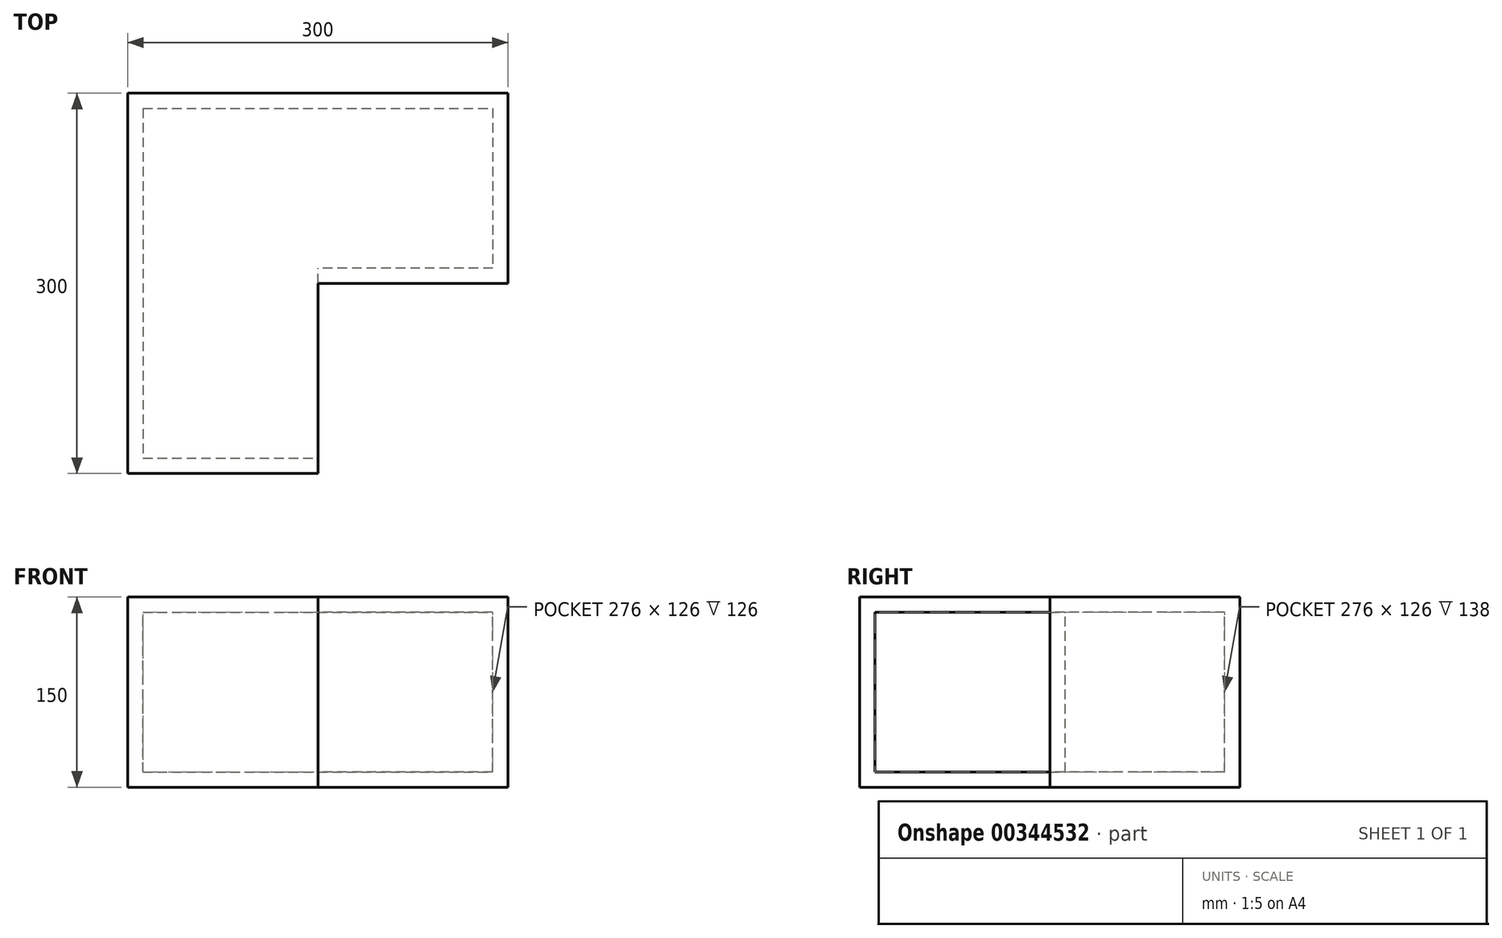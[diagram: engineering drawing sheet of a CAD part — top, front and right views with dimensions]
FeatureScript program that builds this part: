
annotation { "Feature Type Name" : "Feature", "Feature Type Description" : "" }
export const myFeature = defineFeature(function(context is Context, id is Id, definition is map)
    precondition{}
    {
        {
            var Q0;
            Q0=qCreatedBy(makeId("Top.planeOp"),FACE);
            var sketch = newSketch(context, id + "F0", { "sketchPlane" : qUnion([Q0])});
            skLineSegment(sketch, "E0.bottom", {"start": v(-150, 150) * mm, "end": v(150, 150) * mm});
            skLineSegment(sketch, "E0.top", {"start": v(-150, -150) * mm, "end": v(150, -150) * mm});
            skLineSegment(sketch, "E0.left", {"start": v(-150, 150) * mm, "end": v(-150, -150) * mm});
            skLineSegment(sketch, "E0.right", {"start": v(150, 150) * mm, "end": v(150, -150) * mm});
            skPoint(sketch, "E0.middle", {"position": v(0, 0) * mm});
            skLineSegment(sketch, "E1.bottom", {"start": v(150, -150) * mm, "end": v(0, -150) * mm});
            skLineSegment(sketch, "E1.top", {"start": v(150, 0) * mm, "end": v(0, 0) * mm});
            skLineSegment(sketch, "E1.left", {"start": v(150, -150) * mm, "end": v(150, 0) * mm});
            skLineSegment(sketch, "E1.right", {"start": v(0, -150) * mm, "end": v(0, 0) * mm});
            skSolve(sketch);
        }
        {
            var Q0;
            Q0=makeQuery(id+"F0.imprint","IMPRINT",FACE,{"disambiguationData":[TD([[makeQuery(id+"F0.imprint","IMPRINT",EDGE,{"derivedFrom":sQuery(id+"F0.wireOp",EDGE,"E0.bottom")}),-1.0]])]});
            extrude(context, id + "F1", {"entities" : qUnion([Q0]), "oppositeDirection" : true, "depth" : 150 * mm});
        }
        {
            var Q0;
            Q0=makeQuery(id+"F1.opExtrude","SWEPT_FACE",FACE,{"disambiguationData":[OSD([sQuery(id+"F0.wireOp",EDGE,"E1.right")])]});
            shell(context, id + "F2", {"entities" : qUnion([Q0]), "thickness" : 12 * mm});
        }
    });
